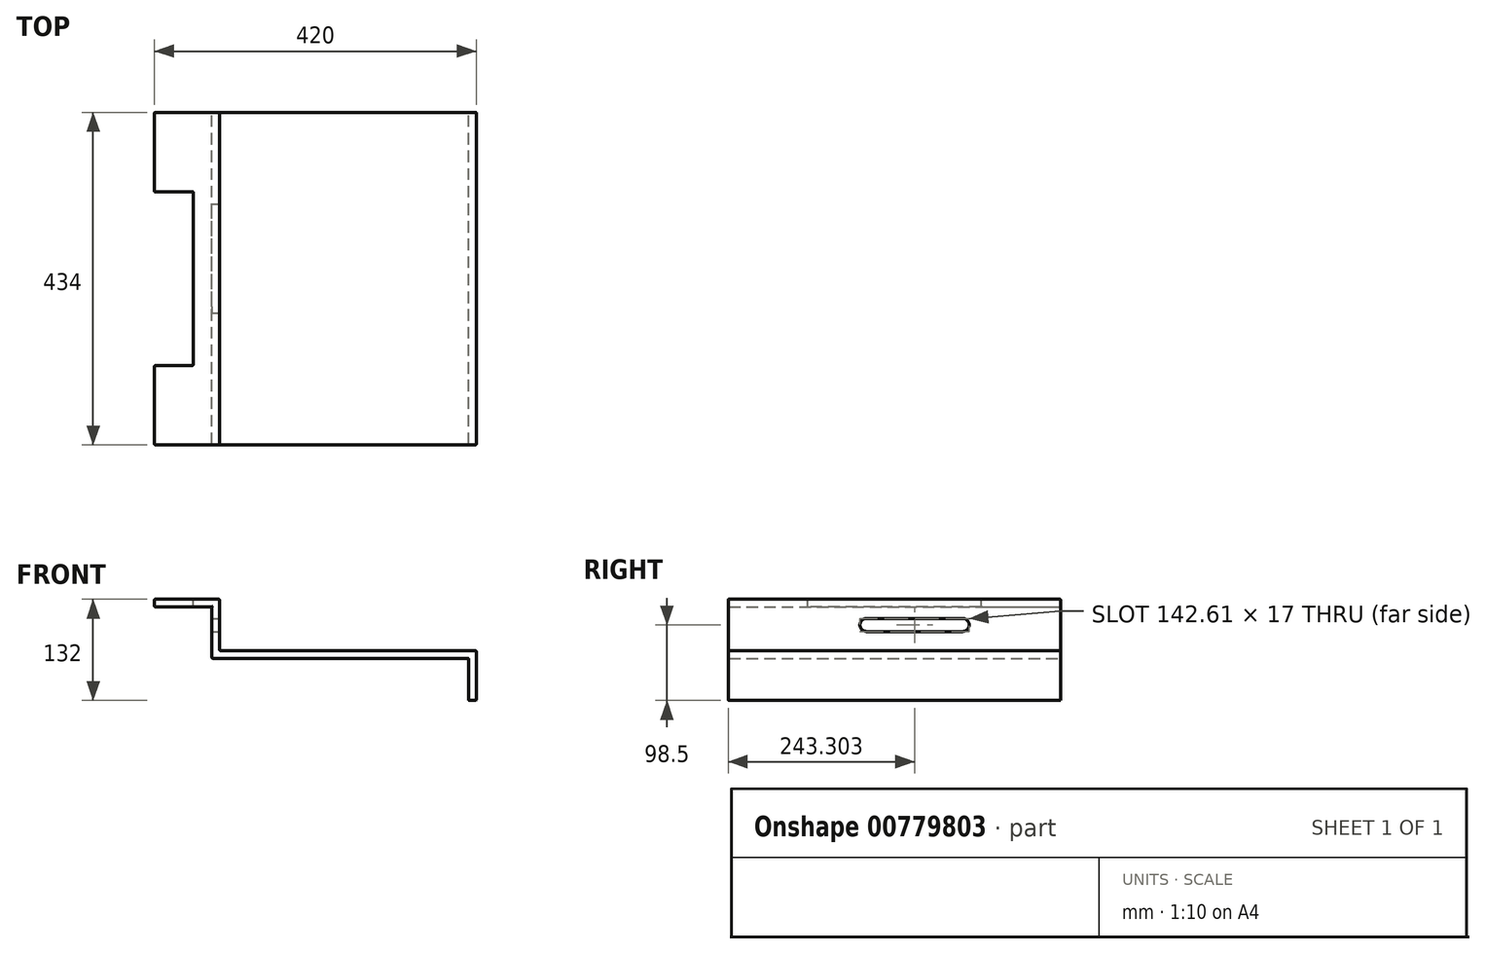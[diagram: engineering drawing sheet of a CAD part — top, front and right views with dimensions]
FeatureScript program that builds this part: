
annotation { "Feature Type Name" : "Feature", "Feature Type Description" : "" }
export const myFeature = defineFeature(function(context is Context, id is Id, definition is map)
    precondition{}
    {
        {
            var Q0;
            Q0=qCreatedBy(makeId("Front.planeOp"),FACE);
            var sketch = newSketch(context, id + "F0", { "sketchPlane" : qUnion([Q0])});
            skLineSegment(sketch, "E0", {"start": v(-218.97, 67) * mm, "end": v(-133.97, 67) * mm});
            skLineSegment(sketch, "E1", {"start": v(-133.97, 67) * mm, "end": v(-133.97, 0) * mm});
            skLineSegment(sketch, "E2", {"start": v(-133.97, 0) * mm, "end": v(201.03, 0) * mm});
            skLineSegment(sketch, "E3", {"start": v(201.03, 0) * mm, "end": v(201.03, -65) * mm});
            skLineSegment(sketch, "E4.0", {"start": v(191.03, -10) * mm, "end": v(191.03, -65) * mm});
            skLineSegment(sketch, "E4.1", {"start": v(-143.97, -10) * mm, "end": v(191.03, -10) * mm});
            skLineSegment(sketch, "E4.2", {"start": v(-143.97, 57) * mm, "end": v(-143.97, -10) * mm});
            skLineSegment(sketch, "E4.3", {"start": v(-218.97, 57) * mm, "end": v(-143.97, 57) * mm});
            skLineSegment(sketch, "E5", {"start": v(-218.97, 67) * mm, "end": v(-218.97, 57) * mm});
            skLineSegment(sketch, "E6", {"start": v(191.03, -65) * mm, "end": v(201.03, -65) * mm});
            skSolve(sketch);
        }
        {
            var Q0;
            Q0=makeQuery(id+"F0.imprint","IMPRINT",FACE,{"disambiguationData":[TD([[makeQuery(id+"F0.imprint","IMPRINT",EDGE,{"derivedFrom":sQuery(id+"F0.wireOp",EDGE,"E0")}),-1.0]])]});
            extrude(context, id + "F1", {"entities" : qUnion([Q0]), "depth" : 434 * mm, "offsetDistance" : 25.4 * mm});
        }
        {
            var Q0;
            Q0=makeQuery(id+"F1.opExtrude","SWEPT_FACE",FACE,{"disambiguationData":[OSD([sQuery(id+"F0.wireOp",EDGE,"E0")])]});
            var sketch = newSketch(context, id + "F2", { "sketchPlane" : qUnion([Q0])});
            skLineSegment(sketch, "E7.bottom", {"start": v(-218.97, -103.5) * mm, "end": v(-168.54, -103.5) * mm});
            skLineSegment(sketch, "E7.top", {"start": v(-218.97, -330.5) * mm, "end": v(-168.54, -330.5) * mm});
            skLineSegment(sketch, "E7.left", {"start": v(-218.97, -103.5) * mm, "end": v(-218.97, -330.5) * mm});
            skLineSegment(sketch, "E7.right", {"start": v(-168.54, -103.5) * mm, "end": v(-168.54, -330.5) * mm});
            skSolve(sketch);
        }
        {
            var Q0;
            Q0=makeQuery(id+"F2.imprint","IMPRINT",FACE,{"disambiguationData":[TD([[makeQuery(id+"F2.imprint","IMPRINT",EDGE,{"derivedFrom":sQuery(id+"F2.wireOp",EDGE,"E7.bottom")}),-1.0]])]});
            extrude(context, id + "F3", {"entities" : qUnion([Q0]), "operationType" : NewBodyOperationType.REMOVE, "endBound" : BoundingType.THROUGH_ALL, "oppositeDirection" : true, "depth" : 25.4 * mm, "offsetDistance" : 25.4 * mm});
        }
        {
            var Q0;
            Q0=makeQuery(id+"F1.opExtrude","SWEPT_FACE",FACE,{"disambiguationData":[OSD([sQuery(id+"F0.wireOp",EDGE,"E1")])]});
            var sketch = newSketch(context, id + "F4", { "sketchPlane" : qUnion([Q0])});
            skPoint(sketch, "E8.firstSnap0", {"position": v(-434, 33.5) * mm});
            skLineSegment(sketch, "E9.bottom", {"start": v(-253.5, 42) * mm, "end": v(-127.9, 42) * mm});
            skLineSegment(sketch, "E9.top", {"start": v(-253.5, 25) * mm, "end": v(-127.9, 25) * mm});
            skLineSegment(sketch, "E9.left", {"start": v(-262, 33.5) * mm, "end": v(-262, 33.5) * mm});
            skLineSegment(sketch, "E9.right", {"start": v(-119.4, 33.5) * mm, "end": v(-119.4, 33.5) * mm});
            skPoint(sketch, "E10.visualSharp", {"position": v(-262, 42) * mm});
            skArc(sketch, "E10.filletArc", {"start": v(-253.5, 42) * mm, "mid": v(-259.51, 39.51) * mm, "end": v(-262, 33.5) * mm});
            skPoint(sketch, "E11.visualSharp", {"position": v(-262, 25) * mm});
            skArc(sketch, "E11.filletArc", {"start": v(-262, 33.5) * mm, "mid": v(-259.51, 27.49) * mm, "end": v(-253.5, 25) * mm});
            skPoint(sketch, "E12.visualSharp", {"position": v(-119.4, 42) * mm});
            skArc(sketch, "E12.filletArc", {"start": v(-119.4, 33.5) * mm, "mid": v(-121.88, 39.51) * mm, "end": v(-127.9, 42) * mm});
            skPoint(sketch, "E13.visualSharp", {"position": v(-119.4, 25) * mm});
            skArc(sketch, "E13.filletArc", {"start": v(-127.9, 25) * mm, "mid": v(-121.88, 27.49) * mm, "end": v(-119.4, 33.5) * mm});
            skSolve(sketch);
        }
        {
            var Q0;
            Q0 = qSketchRegion(id + "F4", true);
            extrude(context, id + "F5", {"entities" : qUnion([Q0]), "operationType" : NewBodyOperationType.REMOVE, "oppositeDirection" : true, "depth" : 25.4 * mm, "offsetDistance" : 25.4 * mm});
        }
        {
            var Q0;
            Q0=makeQuery(id+"F3.boolean.opBoolean","COPY",EDGE,{"derivedFrom":makeQuery(id+"F3.opExtrude","CAP_EDGE",EDGE,{"disambiguationData":[OSD([sQuery(id+"F2.wireOp",EDGE,"E7.bottom")])],"isStart":true})});
            var Q1;
            Q1=makeQuery(id+"F3.boolean.opBoolean","COPY",EDGE,{"derivedFrom":makeQuery(id+"F3.opExtrude","SWEPT_EDGE",EDGE,{"disambiguationData":[OSD([sQuery(id+"F2.wireOp",EDGE,"E7.bottom"),sQuery(id+"F2.wireOp",EDGE,"E7.right")])]})});
            var Q2;
            Q2=makeQuery(id+"F3.boolean.opBoolean","INTERSECT",EDGE,{"derivedFrom":[makeQuery(id+"F1.opExtrude","SWEPT_FACE",FACE,{"disambiguationData":[OSD([sQuery(id+"F0.wireOp",EDGE,"E4.3")])]}),makeQuery(id+"F3.opExtrude","SWEPT_FACE",FACE,{"disambiguationData":[OSD([sQuery(id+"F2.wireOp",EDGE,"E7.right")])]})]});
            var Q3;
            Q3=makeQuery(id+"F3.boolean.opBoolean","COPY",EDGE,{"derivedFrom":makeQuery(id+"F3.opExtrude","CAP_EDGE",EDGE,{"disambiguationData":[OSD([sQuery(id+"F2.wireOp",EDGE,"E7.right")])],"isStart":true})});
            var Q4;
            {var subQ0=sQuery(id+"F0.wireOp",EDGE,"E0");var subQ1=sQuery(id+"F0.wireOp",EDGE,"E5");Q4=makeQuery(id+"F3.boolean.opBoolean","SPLIT",EDGE,{"disambiguationData":[TD([makeQuery(id+"F3.opExtrude","SWEPT_FACE",FACE,{"disambiguationData":[OSD([sQuery(id+"F2.wireOp",EDGE,"E7.bottom")])]})])],"derivedFrom":makeQuery(id+"F1.opExtrude","SWEPT_EDGE",EDGE,{"disambiguationData":[OSD([subQ0,subQ1])]})});}
            var Q5;
            {var subQ0=sQuery(id+"F0.wireOp",EDGE,"E5");var subQ1=sQuery(id+"F0.wireOp",EDGE,"E4.3");Q5=makeQuery(id+"F3.boolean.opBoolean","SPLIT",EDGE,{"disambiguationData":[TD([makeQuery(id+"F3.opExtrude","SWEPT_FACE",FACE,{"disambiguationData":[OSD([sQuery(id+"F2.wireOp",EDGE,"E7.bottom")])]})])],"derivedFrom":makeQuery(id+"F1.opExtrude","SWEPT_EDGE",EDGE,{"disambiguationData":[OSD([subQ1,subQ0])]})});}
            var Q6;
            Q6=makeQuery(id+"F3.boolean.opBoolean","COPY",EDGE,{"derivedFrom":makeQuery(id+"F3.opExtrude","SWEPT_EDGE",EDGE,{"disambiguationData":[OSD([sQuery(id+"F0.wireOp",EDGE,"E0"),sQuery(id+"F0.wireOp",EDGE,"E5"),sQuery(id+"F2.wireOp",EDGE,"E7.bottom"),sQuery(id+"F2.wireOp",EDGE,"E7.left")])]})});
            var Q7;
            Q7=makeQuery(id+"F1.opExtrude","CAP_EDGE",EDGE,{"disambiguationData":[OSD([sQuery(id+"F0.wireOp",EDGE,"E5")])],"isStart":true});
            var Q8;
            Q8=makeQuery(id+"F1.opExtrude","CAP_EDGE",EDGE,{"disambiguationData":[OSD([sQuery(id+"F0.wireOp",EDGE,"E0")])],"isStart":true});
            var Q9;
            Q9=makeQuery(id+"F1.opExtrude","SWEPT_EDGE",EDGE,{"disambiguationData":[OSD([sQuery(id+"F0.wireOp",EDGE,"E0"),sQuery(id+"F0.wireOp",EDGE,"E1")])]});
            var Q10;
            {var subQ0=sQuery(id+"F0.wireOp",EDGE,"E0");var subQ1=sQuery(id+"F0.wireOp",EDGE,"E5");Q10=makeQuery(id+"F3.boolean.opBoolean","SPLIT",EDGE,{"disambiguationData":[TD([makeQuery(id+"F3.opExtrude","SWEPT_FACE",FACE,{"disambiguationData":[OSD([sQuery(id+"F2.wireOp",EDGE,"E7.top")])]})])],"derivedFrom":makeQuery(id+"F1.opExtrude","SWEPT_EDGE",EDGE,{"disambiguationData":[OSD([subQ0,subQ1])]})});}
            var Q11;
            {var subQ0=sQuery(id+"F0.wireOp",EDGE,"E5");var subQ1=sQuery(id+"F0.wireOp",EDGE,"E4.3");Q11=makeQuery(id+"F3.boolean.opBoolean","SPLIT",EDGE,{"disambiguationData":[TD([makeQuery(id+"F3.opExtrude","SWEPT_FACE",FACE,{"disambiguationData":[OSD([sQuery(id+"F2.wireOp",EDGE,"E7.top")])]})])],"derivedFrom":makeQuery(id+"F1.opExtrude","SWEPT_EDGE",EDGE,{"disambiguationData":[OSD([subQ1,subQ0])]})});}
            var Q12;
            Q12=makeQuery(id+"F3.boolean.opBoolean","COPY",EDGE,{"derivedFrom":makeQuery(id+"F3.opExtrude","SWEPT_EDGE",EDGE,{"disambiguationData":[OSD([sQuery(id+"F0.wireOp",EDGE,"E0"),sQuery(id+"F0.wireOp",EDGE,"E5"),sQuery(id+"F2.wireOp",EDGE,"E7.top"),sQuery(id+"F2.wireOp",EDGE,"E7.left")])]})});
            var Q13;
            Q13=makeQuery(id+"F3.boolean.opBoolean","INTERSECT",EDGE,{"derivedFrom":[makeQuery(id+"F1.opExtrude","SWEPT_FACE",FACE,{"disambiguationData":[OSD([sQuery(id+"F0.wireOp",EDGE,"E4.3")])]}),makeQuery(id+"F3.opExtrude","SWEPT_FACE",FACE,{"disambiguationData":[OSD([sQuery(id+"F2.wireOp",EDGE,"E7.top")])]})]});
            var Q14;
            Q14=makeQuery(id+"F3.boolean.opBoolean","COPY",EDGE,{"derivedFrom":makeQuery(id+"F3.opExtrude","CAP_EDGE",EDGE,{"disambiguationData":[OSD([sQuery(id+"F2.wireOp",EDGE,"E7.top")])],"isStart":true})});
            var Q15;
            Q15=makeQuery(id+"F3.boolean.opBoolean","COPY",EDGE,{"derivedFrom":makeQuery(id+"F3.opExtrude","SWEPT_EDGE",EDGE,{"disambiguationData":[OSD([sQuery(id+"F2.wireOp",EDGE,"E7.top"),sQuery(id+"F2.wireOp",EDGE,"E7.right")])]})});
            var Q16;
            Q16=makeQuery(id+"F1.opExtrude","CAP_EDGE",EDGE,{"disambiguationData":[OSD([sQuery(id+"F0.wireOp",EDGE,"E0")])],"isStart":false});
            var Q17;
            Q17=makeQuery(id+"F1.opExtrude","CAP_EDGE",EDGE,{"disambiguationData":[OSD([sQuery(id+"F0.wireOp",EDGE,"E5")])],"isStart":false});
            var Q18;
            Q18=makeQuery(id+"F1.opExtrude","CAP_EDGE",EDGE,{"disambiguationData":[OSD([sQuery(id+"F0.wireOp",EDGE,"E4.3")])],"isStart":false});
            var Q19;
            Q19=makeQuery(id+"F1.opExtrude","CAP_EDGE",EDGE,{"disambiguationData":[OSD([sQuery(id+"F0.wireOp",EDGE,"E4.2")])],"isStart":false});
            var Q20;
            Q20=makeQuery(id+"F1.opExtrude","CAP_EDGE",EDGE,{"disambiguationData":[OSD([sQuery(id+"F0.wireOp",EDGE,"E1")])],"isStart":false});
            var Q21;
            Q21=makeQuery(id+"F1.opExtrude","SWEPT_EDGE",EDGE,{"disambiguationData":[OSD([sQuery(id+"F0.wireOp",EDGE,"E4.1"),sQuery(id+"F0.wireOp",EDGE,"E4.2")])]});
            var Q22;
            Q22=makeQuery(id+"F1.opExtrude","CAP_EDGE",EDGE,{"disambiguationData":[OSD([sQuery(id+"F0.wireOp",EDGE,"E4.2")])],"isStart":true});
            var Q23;
            Q23=makeQuery(id+"F1.opExtrude","CAP_EDGE",EDGE,{"disambiguationData":[OSD([sQuery(id+"F0.wireOp",EDGE,"E1")])],"isStart":true});
            var Q24;
            Q24=makeQuery(id+"F1.opExtrude","CAP_EDGE",EDGE,{"disambiguationData":[OSD([sQuery(id+"F0.wireOp",EDGE,"E2")])],"isStart":true});
            var Q25;
            Q25=makeQuery(id+"F1.opExtrude","CAP_EDGE",EDGE,{"disambiguationData":[OSD([sQuery(id+"F0.wireOp",EDGE,"E4.1")])],"isStart":true});
            var Q26;
            Q26=makeQuery(id+"F1.opExtrude","CAP_EDGE",EDGE,{"disambiguationData":[OSD([sQuery(id+"F0.wireOp",EDGE,"E4.3")])],"isStart":true});
            var Q27;
            Q27=makeQuery(id+"F1.opExtrude","CAP_EDGE",EDGE,{"disambiguationData":[OSD([sQuery(id+"F0.wireOp",EDGE,"E2")])],"isStart":false});
            var Q28;
            Q28=makeQuery(id+"F1.opExtrude","CAP_EDGE",EDGE,{"disambiguationData":[OSD([sQuery(id+"F0.wireOp",EDGE,"E4.1")])],"isStart":false});
            var Q29;
            Q29=makeQuery(id+"F1.opExtrude","SWEPT_EDGE",EDGE,{"disambiguationData":[OSD([sQuery(id+"F0.wireOp",EDGE,"E1"),sQuery(id+"F0.wireOp",EDGE,"E2")])]});
            var Q30;
            Q30=makeQuery(id+"F1.opExtrude","SWEPT_EDGE",EDGE,{"disambiguationData":[OSD([sQuery(id+"F0.wireOp",EDGE,"E2"),sQuery(id+"F0.wireOp",EDGE,"E3")])]});
            var Q31;
            Q31=makeQuery(id+"F1.opExtrude","CAP_EDGE",EDGE,{"disambiguationData":[OSD([sQuery(id+"F0.wireOp",EDGE,"E3")])],"isStart":false});
            var Q32;
            Q32=makeQuery(id+"F1.opExtrude","CAP_EDGE",EDGE,{"disambiguationData":[OSD([sQuery(id+"F0.wireOp",EDGE,"E4.0")])],"isStart":false});
            var Q33;
            Q33=makeQuery(id+"F1.opExtrude","CAP_EDGE",EDGE,{"disambiguationData":[OSD([sQuery(id+"F0.wireOp",EDGE,"E6")])],"isStart":false});
            var Q34;
            Q34=makeQuery(id+"F1.opExtrude","SWEPT_EDGE",EDGE,{"disambiguationData":[OSD([sQuery(id+"F0.wireOp",EDGE,"E3"),sQuery(id+"F0.wireOp",EDGE,"E6")])]});
            var Q35;
            Q35=makeQuery(id+"F1.opExtrude","SWEPT_EDGE",EDGE,{"disambiguationData":[OSD([sQuery(id+"F0.wireOp",EDGE,"E4.0"),sQuery(id+"F0.wireOp",EDGE,"E6")])]});
            var Q36;
            Q36=makeQuery(id+"F1.opExtrude","CAP_EDGE",EDGE,{"disambiguationData":[OSD([sQuery(id+"F0.wireOp",EDGE,"E3")])],"isStart":true});
            var Q37;
            Q37=makeQuery(id+"F1.opExtrude","CAP_EDGE",EDGE,{"disambiguationData":[OSD([sQuery(id+"F0.wireOp",EDGE,"E4.0")])],"isStart":true});
            var Q38;
            Q38=makeQuery(id+"F1.opExtrude","SWEPT_EDGE",EDGE,{"disambiguationData":[OSD([sQuery(id+"F0.wireOp",EDGE,"E4.0"),sQuery(id+"F0.wireOp",EDGE,"E4.1")])]});
            fillet(context, id + "F6", {"entities" : qUnion([Q0, Q1, Q2, Q3, Q4, Q5, Q6, Q7, Q8, Q9, Q10, Q11, Q12, Q13, Q14, Q15, Q16, Q17, Q18, Q19, Q20, Q21, Q22, Q23, Q24, Q25, Q26, Q27, Q28, Q29, Q30, Q31, Q32, Q33, Q34, Q35, Q36, Q37, Q38]), "radius" : 1 * mm, "tangentPropagation" : true, "allowEdgeOverflow" : false});
        }
    });
